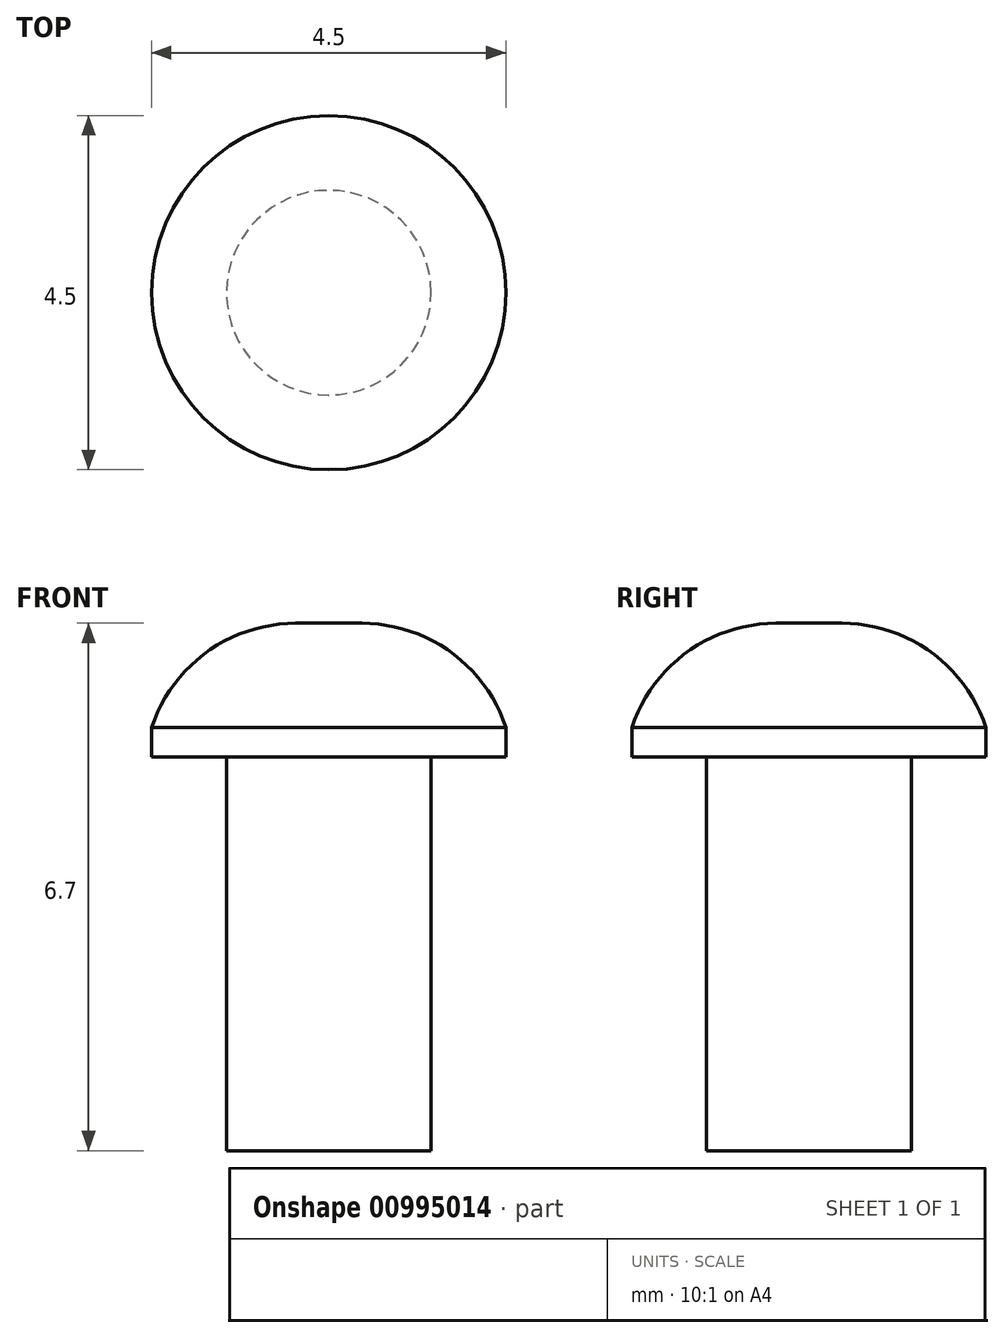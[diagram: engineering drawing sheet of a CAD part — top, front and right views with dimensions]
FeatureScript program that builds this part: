
annotation { "Feature Type Name" : "Feature", "Feature Type Description" : "" }
export const myFeature = defineFeature(function(context is Context, id is Id, definition is map)
    precondition{}
    {
        {
            var Q0;
            Q0=qCreatedBy(makeId("Front.planeOp"),FACE);
            var sketch = newSketch(context, id + "F0", { "sketchPlane" : qUnion([Q0])});
            skLineSegment(sketch, "E0", {"start": v(0, 0) * mm, "end": v(2.25, 0) * mm});
            skLineSegment(sketch, "E1", {"start": v(0, 1.7) * mm, "end": v(0.42, 1.7) * mm});
            skLineSegment(sketch, "E2", {"start": v(2.25, 0) * mm, "end": v(2.25, 0.37) * mm});
            skArc(sketch, "E3", {"start": v(2.25, 0.37) * mm, "mid": v(1.55, 1.33) * mm, "end": v(0.42, 1.7) * mm});
            skLineSegment(sketch, "E4", {"start": v(0, 1.7) * mm, "end": v(0, 0) * mm});
            skSolve(sketch);
        }
        {
            var Q0;
            Q0=qSketchRegion(id+"F0",true);
            var Q1;
            Q1=sQuery(id+"F0.wireOp",EDGE,"E4");
            revolve(context, id + "F1", {"surfaceOperationType" : NewSurfaceOperationType.NEW, "entities" : qUnion([Q0]), "axis" : qUnion([Q1]), "revolveType" : RevolveType.FULL});
        }
        {
            var Q0;
            Q0=makeQuery(id+"F1.opRevolve","SWEPT_FACE",FACE,{"disambiguationData":[OSD([sQuery(id+"F0.wireOp",EDGE,"E0")])]});
            var sketch = newSketch(context, id + "F2", { "sketchPlane" : qUnion([Q0])});
            skCircle(sketch, "E5", {"center": v(0, 0) * mm, "radius": 1.3 * mm});
            skSolve(sketch);
        }
        {
            var Q0;
            Q0=qSketchRegion(id+"F2",true);
            extrude(context, id + "F3", {"entities" : qUnion([Q0]), "operationType" : NewBodyOperationType.ADD, "depth" : 5 * mm, "offsetDistance" : 25 * mm});
        }
    });
